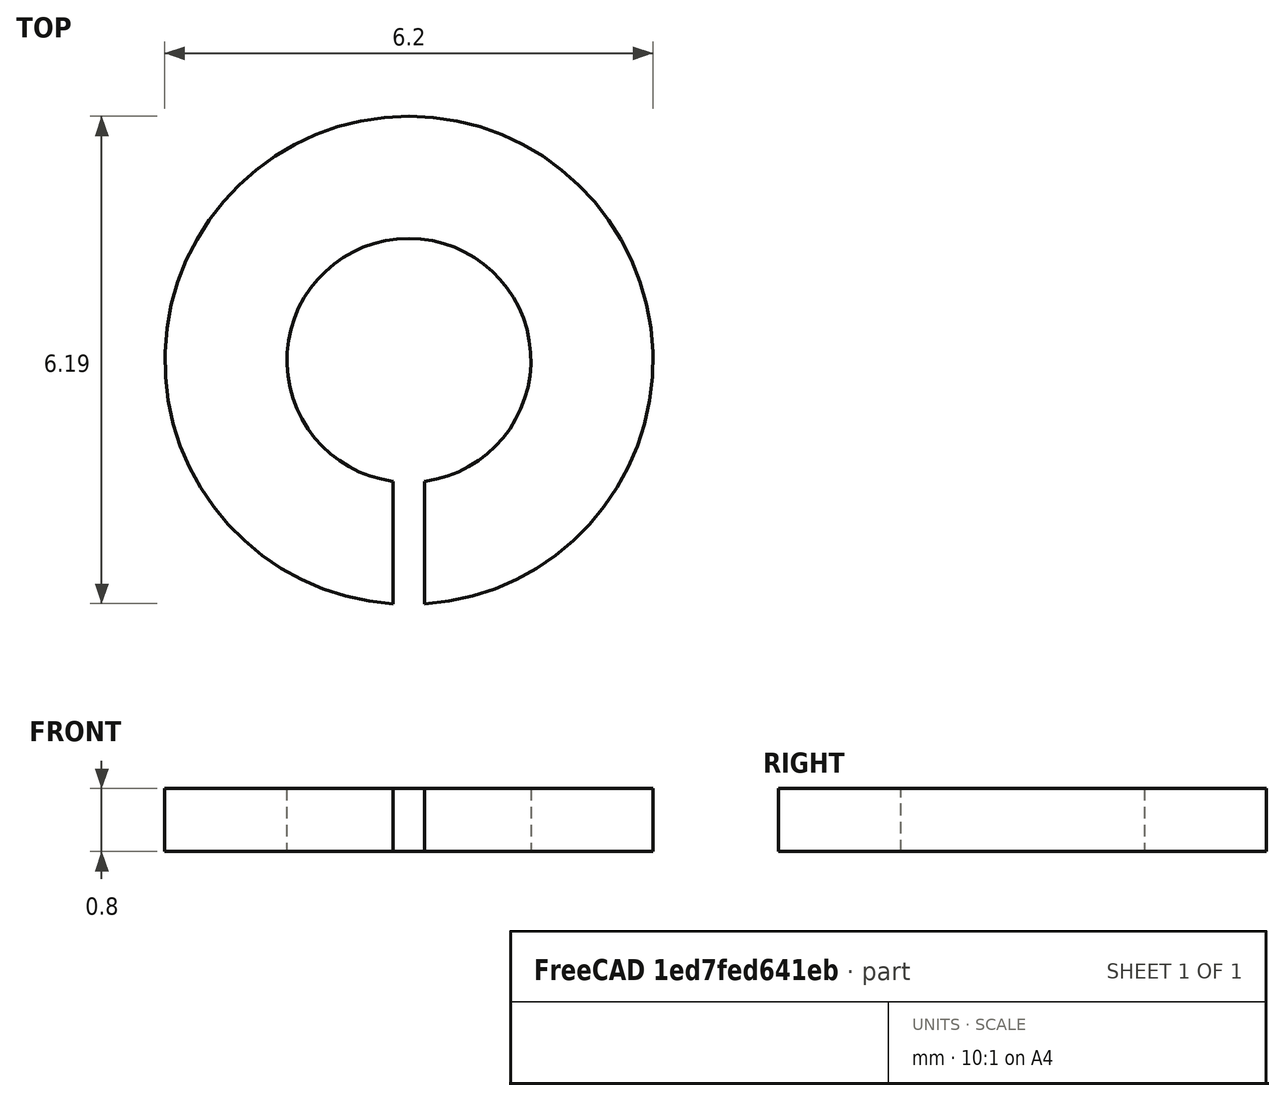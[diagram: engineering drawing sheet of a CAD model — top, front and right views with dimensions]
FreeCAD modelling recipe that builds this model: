
FCSTD DOCUMENT  (FreeCAD 0.15R4651 (Git))
Label: Federring_DIN127-B3
License: All rights reserved
LicenseURL: http://de.wikipedia.org/wiki/Alle_Rechte_vorbehalten
objects: Sketcher::SketchObject×1, PartDesign::Pad×1
note: 3 computed .brp shape members not serialized (recipe doc carries the construction recipe); baked Part::Feature solids carry a one-line shape summary decoded from their .brp

FEATURE [Sketcher::SketchObject] Sketch
  sketch-geometry (4):
    g0: ArcOfCircle CenterX=0 CenterY=0 CenterZ=0 NormalX=0 NormalY=0 NormalZ=1 Radius=1.55 StartAngle=4.84178 EndAngle=10.8662
    g1: ArcOfCircle CenterX=0 CenterY=0 CenterZ=0 NormalX=0 NormalY=0 NormalZ=1 Radius=3.1 StartAngle=4.77695 EndAngle=10.931
    g2: LineSegment StartX=0.2 StartY=-1.53704 StartZ=0 EndX=0.2 EndY=-3.09354 EndZ=0
    g3: LineSegment StartX=-0.2 StartY=-3.09354 StartZ=0 EndX=-0.2 EndY=-1.53704 EndZ=0
  constraints (12):
    c: Coincident(g0,g-1)
    c: Coincident(g1,g-1)
    c: Vertical(g2)
    c: Vertical(g3)
    c: Coincident(g0,g2)
    c: Coincident(g0,g3)
    c: Coincident(g1,g2)
    c: Coincident(g1,g3)
    c: Symmetric(g1,g1,g-2)
    c: Radius(g0) = 1.55
    c: Radius(g1) = 3.1
    c: DistanceX(g1,g1) = -0.4
FEATURE [PartDesign::Pad] Pad  label="Federring DIN 127-B 3 #"
  Length = 0.8
  Length2 = 100
  Midplane = true
  Sketch = -> Sketch
  Type = 0
